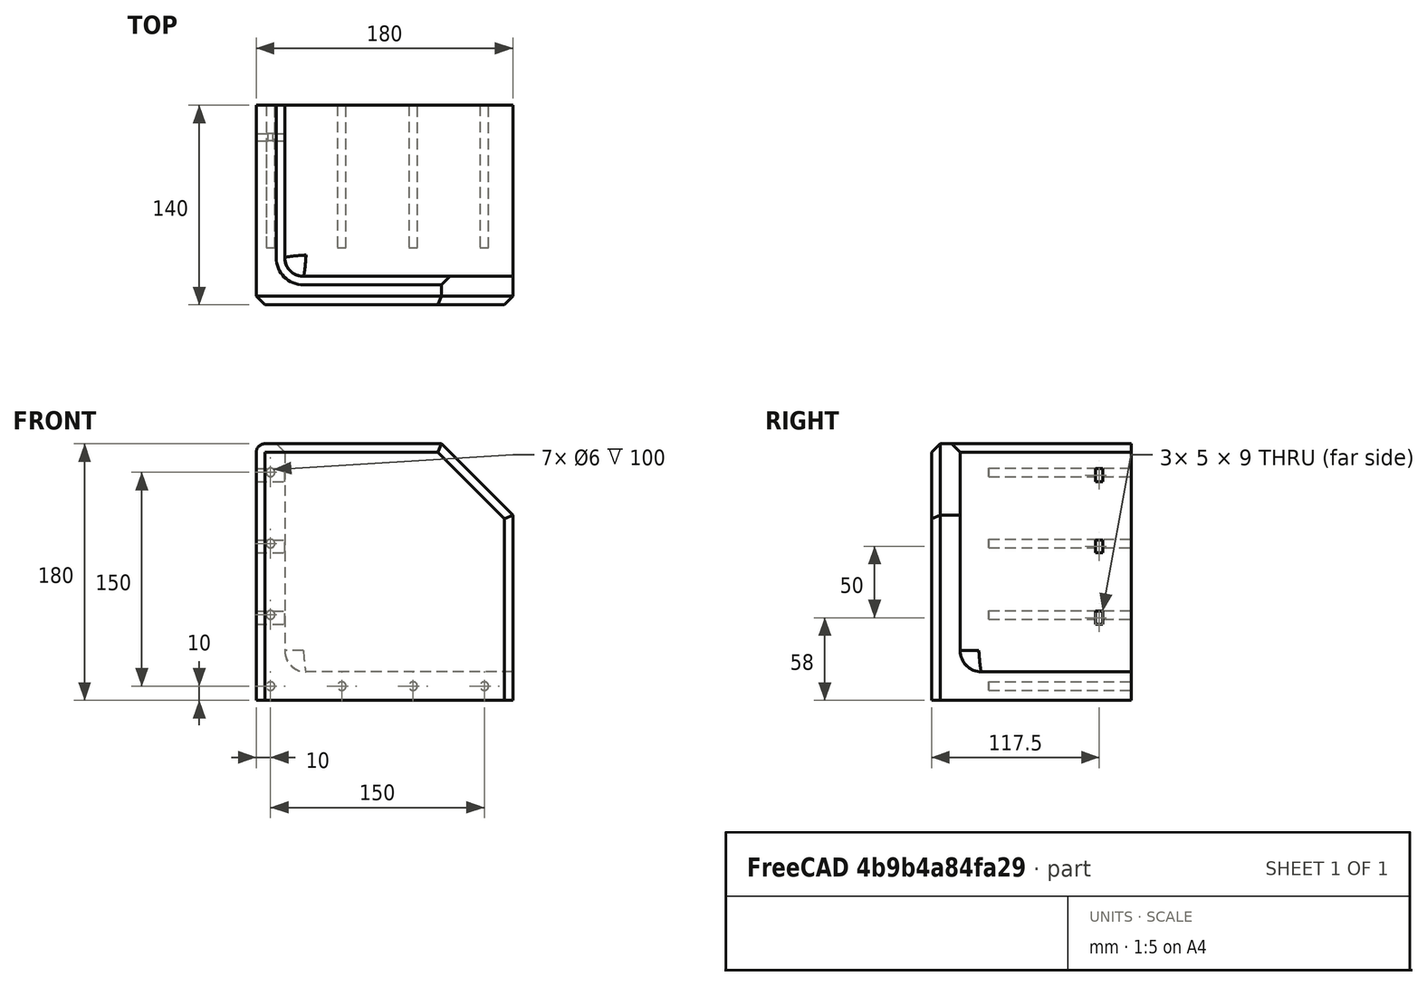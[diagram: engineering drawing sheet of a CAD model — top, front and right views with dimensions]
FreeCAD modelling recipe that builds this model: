
FCSTD DOCUMENT  (FreeCAD 0.19R)
Label: BassoonClip
License: All rights reserved
LicenseURL: http://en.wikipedia.org/wiki/All_rights_reserved
objects: Sketcher::SketchObject×5, PartDesign::Pocket×3, PartDesign::Chamfer×3, PartDesign::Fillet×3, PartDesign::Pad×1, PartDesign::Body×1, Mesh::Feature×1
note: 26 computed .brp shape members not serialized (recipe doc carries the construction recipe); baked Part::Feature solids carry a one-line shape summary decoded from their .brp

FEATURE [Sketcher::SketchObject] Sketch
  FullyConstrained = true
  MapMode = 5
  Support = -> [XY_Plane]
  sketch-geometry (4):
    g0: LineSegment StartX=0 StartY=0 StartZ=0 EndX=180 EndY=0 EndZ=0
    g1: LineSegment StartX=180 StartY=0 StartZ=0 EndX=180 EndY=-140 EndZ=0
    g2: LineSegment StartX=180 StartY=-140 StartZ=0 EndX=0 EndY=-140 EndZ=0
    g3: LineSegment StartX=0 StartY=-140 StartZ=0 EndX=0 EndY=0 EndZ=0
  constraints (11):
    c: Coincident(g0,g1)
    c: Coincident(g1,g2)
    c: Coincident(g2,g3)
    c: Coincident(g3,g0)
    c: Horizontal(g0)
    c: Horizontal(g2)
    c: Vertical(g1)
    c: Vertical(g3)
    c: Coincident(g0,g-1)
    c: Distance(g0) = 180
    c: Distance(g3) = 140
FEATURE [PartDesign::Pad] Pad
  Direction = (1,1,1)
  Length = 180
  Length2 = 100
  Profile = -> Sketch
  Type = 0
FEATURE [Sketcher::SketchObject] Sketch001
  FullyConstrained = false
  MapMode = 5
  Placement = pos=(0,0,180) rot=(0,0,1;0rad)
  Support = -> [Pad]
  sketch-geometry (4):
    g0: LineSegment StartX=20 StartY=37.7964 StartZ=0 EndX=236.81 EndY=37.7964 EndZ=0
    g1: LineSegment StartX=236.81 StartY=37.7964 StartZ=0 EndX=236.81 EndY=-120 EndZ=0
    g2: LineSegment StartX=236.81 StartY=-120 StartZ=0 EndX=20 EndY=-120 EndZ=0
    g3: LineSegment StartX=20 StartY=-120 StartZ=0 EndX=20 EndY=37.7964 EndZ=0
  constraints (10):
    c: Coincident(g0,g1)
    c: Coincident(g1,g2)
    c: Coincident(g2,g3)
    c: Coincident(g3,g0)
    c: Horizontal(g0)
    c: Horizontal(g2)
    c: Vertical(g1)
    c: Vertical(g3)
    c: DistanceX(g0) = 20
    c: DistanceY(g1) = -120
FEATURE [PartDesign::Pocket] Pocket
  BaseFeature = -> Pad
  Length = 160
  Length2 = 100
  Profile = -> Sketch001
  Type = 0
FEATURE [PartDesign::Chamfer] Chamfer
  Angle = 45
  Base = -> Pocket [Edge11]
  BaseFeature = -> Pocket
  ChamferType = 0
  FlipDirection = false
  Size = 50
  Size2 = 1
  SupportTransform = false
FEATURE [Sketcher::SketchObject] Sketch002
  FullyConstrained = false
  MapMode = 5
  Placement = pos=(0,0,0) rot=(0,0.707107,0.707107;3.14159rad)
  Support = -> [Chamfer]
  sketch-geometry (9):
    g0: Circle CenterX=-10 CenterY=160 CenterZ=0 NormalX=0 NormalY=0 NormalZ=1 AngleXU=0 Radius=3
    g1: Circle CenterX=-10 CenterY=110 CenterZ=0 NormalX=0 NormalY=0 NormalZ=1 AngleXU=0 Radius=3
    g2: Circle CenterX=-10 CenterY=60 CenterZ=0 NormalX=0 NormalY=0 NormalZ=1 AngleXU=0 Radius=3
    g3: Circle CenterX=-160 CenterY=10 CenterZ=0 NormalX=0 NormalY=0 NormalZ=1 AngleXU=0 Radius=3
    g4: Circle CenterX=-110 CenterY=10 CenterZ=0 NormalX=0 NormalY=0 NormalZ=1 AngleXU=0 Radius=3
    g5: Circle CenterX=-10 CenterY=10 CenterZ=0 NormalX=0 NormalY=0 NormalZ=1 AngleXU=0 Radius=3
    g6: Circle CenterX=-60 CenterY=10 CenterZ=0 NormalX=0 NormalY=0 NormalZ=1 AngleXU=0 Radius=3
    g7: LineSegment StartX=-10 StartY=182.376 StartZ=0 EndX=-10 EndY=-26.7 EndZ=0
    g8: LineSegment StartX=-203.84 StartY=10 StartZ=0 EndX=19.4984 EndY=10 EndZ=0
  constraints (25):
    c: Vertical(g7)
    c: Horizontal(g8)
    c: PointOnObject(g3,g8)
    c: PointOnObject(g4,g8)
    c: PointOnObject(g6,g8)
    c: PointOnObject(g5,g8)
    c: PointOnObject(g5,g7)
    c: PointOnObject(g2,g7)
    c: PointOnObject(g1,g7)
    c: PointOnObject(g0,g7)
    c: Diameter(g0) = 6
    c: Equal(g0,g1)
    c: Equal(g0,g2)
    c: Equal(g0,g5)
    c: Equal(g0,g6)
    c: Equal(g0,g4)
    c: Equal(g0,g3)
    c: Distance(g5,g6) = 50
    c: Distance(g4,g6) = 50
    c: Distance(g4,g3) = 50
    c: Distance(g5,g2) = 50
    c: Distance(g2,g1) = 50
    c: Distance(g1,g0) = 50
    c: DistanceY(g8) = 10
    c: DistanceX(g7) = -10
FEATURE [PartDesign::Pocket] Pocket001
  BaseFeature = -> Chamfer
  Length = 100
  Length2 = 100
  Profile = -> Sketch002
  Type = 0
FEATURE [Sketcher::SketchObject] Sketch003
  FullyConstrained = true
  MapMode = 5
  Placement = pos=(0,0,0) rot=(0.57735,-0.57735,-0.57735;2.0944rad)
  Support = -> [Pocket001]
FEATURE [Sketcher::SketchObject] Sketch004
  FullyConstrained = false
  MapMode = 5
  Placement = pos=(0,0,0) rot=(0.57735,-0.57735,-0.57735;2.0944rad)
  Support = -> [Pocket001]
  sketch-geometry (13):
    g0: LineSegment StartX=20 StartY=162.5 StartZ=0 EndX=25 EndY=162.5 EndZ=0
    g1: LineSegment StartX=25 StartY=162.5 StartZ=0 EndX=25 EndY=153.5 EndZ=0
    g2: LineSegment StartX=25 StartY=153.5 StartZ=0 EndX=20 EndY=153.5 EndZ=0
    g3: LineSegment StartX=20 StartY=153.5 StartZ=0 EndX=20 EndY=162.5 EndZ=0
    g4: LineSegment StartX=20 StartY=112.5 StartZ=0 EndX=25 EndY=112.5 EndZ=0
    g5: LineSegment StartX=25 StartY=112.5 StartZ=0 EndX=25 EndY=103.5 EndZ=0
    g6: LineSegment StartX=25 StartY=103.5 StartZ=0 EndX=20 EndY=103.5 EndZ=0
    g7: LineSegment StartX=20 StartY=103.5 StartZ=0 EndX=20 EndY=112.5 EndZ=0
    g8: LineSegment StartX=20 StartY=62.5 StartZ=0 EndX=25 EndY=62.5 EndZ=0
    g9: LineSegment StartX=25 StartY=62.5 StartZ=0 EndX=25 EndY=53.5 EndZ=0
    g10: LineSegment StartX=25 StartY=53.5 StartZ=0 EndX=20 EndY=53.5 EndZ=0
    g11: LineSegment StartX=20 StartY=53.5 StartZ=0 EndX=20 EndY=62.5 EndZ=0
    g12: LineSegment StartX=20 StartY=190.139 StartZ=0 EndX=20 EndY=-39.1873 EndZ=0
  constraints (38):
    c: Coincident(g0,g1)
    c: Coincident(g1,g2)
    c: Coincident(g2,g3)
    c: Coincident(g3,g0)
    c: Horizontal(g0)
    c: Horizontal(g2)
    c: Vertical(g1)
    c: Vertical(g3)
    c: Coincident(g4,g5)
    c: Coincident(g5,g6)
    c: Coincident(g6,g7)
    c: Coincident(g7,g4)
    c: Horizontal(g4)
    c: Horizontal(g6)
    c: Vertical(g5)
    c: Vertical(g7)
    c: Coincident(g8,g9)
    c: Coincident(g9,g10)
    c: Coincident(g10,g11)
    c: Coincident(g11,g8)
    c: Horizontal(g8)
    c: Horizontal(g10)
    c: Vertical(g9)
    c: Vertical(g11)
    c: Equal(g0,g4)
    c: Equal(g4,g8)
    c: Equal(g1,g5)
    c: Equal(g5,g9)
    c: Distance(g1) = 9
    c: Vertical(g12)
    c: PointOnObject(g0,g12)
    c: PointOnObject(g4,g12)
    c: PointOnObject(g8,g12)
    c: Distance(g8,g4) = 50
    c: Distance(g4,g0) = 50
    c: DistanceY(g9) = 53.5
    c: DistanceX(g10) = 20
    c: Distance(g0) = 5
FEATURE [PartDesign::Pocket] Pocket002
  BaseFeature = -> Pocket001
  Length = 5
  Length2 = 100
  Profile = -> Sketch004
  Type = 1
FEATURE [PartDesign::Fillet] Fillet
  Base = -> Pocket002 [Edge16]
  BaseFeature = -> Pocket002
  Radius = 13
  SupportTransform = false
FEATURE [PartDesign::Fillet] Fillet001
  Base = -> Fillet [Edge4]
  BaseFeature = -> Fillet
  Radius = 15
  SupportTransform = false
FEATURE [PartDesign::Fillet] Fillet002
  Base = -> Fillet001 [Edge16]
  BaseFeature = -> Fillet001
  Radius = 6
  SupportTransform = false
FEATURE [PartDesign::Chamfer] Chamfer001
  Angle = 45
  Base = -> Fillet002 [Edge6]
  BaseFeature = -> Fillet002
  ChamferType = 0
  FlipDirection = false
  Size = 6
  Size2 = 1
  SupportTransform = false
FEATURE [PartDesign::Chamfer] Chamfer002
  Angle = 45
  Base = -> Chamfer001 [Edge16,Edge11,Edge3,Edge15]
  BaseFeature = -> Chamfer001
  ChamferType = 0
  FlipDirection = false
  Size = 6
  Size2 = 1
  SupportTransform = false
FEATURE [PartDesign::Body] Body
  Group = -> [Sketch,Pad,Sketch001,Pocket,Chamfer,Sketch002,Pocket001,Sketch003,Sketch004,Pocket002,Fillet,Fillet001,Fillet002,Chamfer001,Chamfer002]
  Origin = -> Origin
  Tip = -> Chamfer002
FEATURE [Mesh::Feature] Mesh  label="Chamfer002 (Meshed)"
